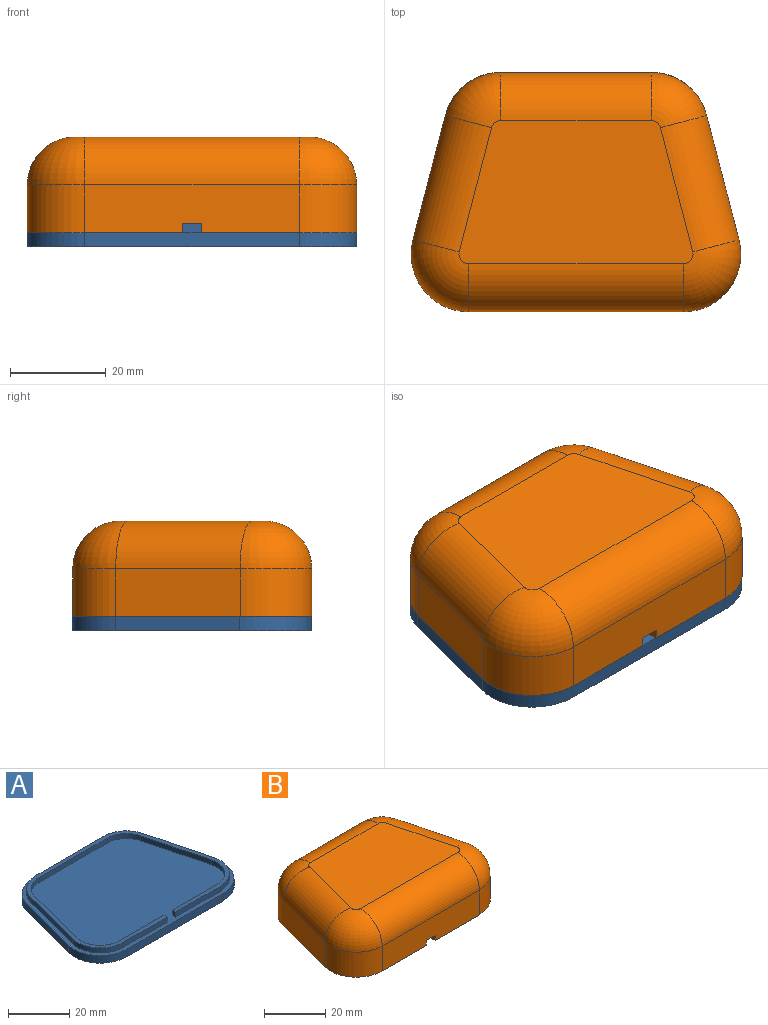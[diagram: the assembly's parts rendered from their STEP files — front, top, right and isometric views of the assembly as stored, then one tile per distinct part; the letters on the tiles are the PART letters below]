
ASSEMBLY  parts=2 mates=1
PART A: 31 faces, bbox 69x50x5 mm
  f0: plane 20.48x2mm, normal (0,-1,0), area 41mm2, adj f2,f12,f14,f30
  f1: plane 20.48x2mm, normal (0,1,0), area 41mm2, adj f2,f12,f26,f29
  f2: plane 65.96x47mm, normal (0,0,1), area 281.1mm2, adj f0,f1,f13,f14,f15,f16,f17,f18
  f3: plane 26x6.76mm, normal (0.97,0.25,0), area 80.6mm2, adj f4,f10,f11,f12
  f4: cylinder r=12mm len=11.61mm, axis (0,0,1), area 47.4mm2, adj f3,f5,f11,f12
  f5: plane 31.44x3mm, normal (0,1,0), area 94.3mm2, adj f4,f6,f11,f12
  f6: cylinder r=12mm len=11.61mm, axis (0,0,1), area 47.4mm2, adj f5,f7,f11,f12
  f7: plane 26x6.76mm, normal (-0.97,0.25,0), area 80.6mm2, adj f6,f8,f11,f12
  f8: cylinder r=12mm len=15.02mm, axis (0,0,1), area 65.7mm2, adj f7,f9,f11,f12
  f9: plane 44.96x3mm, normal (0,-1,0), area 134.9mm2, adj f8,f10,f11,f12
  f10: cylinder r=12mm len=15.02mm, axis (0,0,1), area 65.7mm2, adj f3,f9,f11,f12
  f11: plane 68.96x50mm, normal (0,0,-1), area 3007.2mm2, adj f3,f4,f5,f6,f7,f8,f9,f10
  f12: plane 68.96x50mm, normal (0,0,1), area 2726.1mm2, adj f0,f1,f3,f4,f5,f6,f7,f8
  f13: plane 26x6.76mm, normal (-0.97,0.25,0), area 53.7mm2, adj f2,f12,f14,f28
  f14: cylinder r=10.5mm len=13.14mm, axis (0,0,1), area 38.3mm2, adj f0,f2,f12,f13
  f15: plane 20.48x2mm, normal (0,-1,0), area 41mm2, adj f2,f12,f16,f29
  f16: cylinder r=10.5mm len=13.14mm, axis (0,0,1), area 38.3mm2, adj f2,f12,f15,f17
  f17: plane 26x6.76mm, normal (0.97,0.25,0), area 53.7mm2, adj f2,f12,f16,f18
  f18: cylinder r=10.5mm len=10.16mm, axis (0,0,1), area 27.6mm2, adj f2,f12,f17,f19
  f19: plane 31.44x2mm, normal (0,1,0), area 62.9mm2, adj f2,f12,f18,f28
  f20: cylinder r=9mm len=11.26mm, axis (0,0,1), area 32.9mm2, adj f2,f12,f21,f27
  f21: plane 26x6.76mm, normal (0.97,-0.25,0), area 53.7mm2, adj f2,f12,f20,f22
  f22: cylinder r=9mm len=8.71mm, axis (0,0,1), area 23.7mm2, adj f2,f12,f21,f23
  f23: plane 31.44x2mm, normal (0,-1,0), area 62.9mm2, adj f2,f12,f22,f24
  f24: cylinder r=9mm len=8.71mm, axis (0,0,1), area 23.7mm2, adj f2,f12,f23,f25
  f25: plane 26x6.76mm, normal (-0.97,-0.25,0), area 53.7mm2, adj f2,f12,f24,f26
  f26: cylinder r=9mm len=11.26mm, axis (0,0,1), area 32.9mm2, adj f1,f2,f12,f25
  f27: plane 20.48x2mm, normal (0,1,0), area 41mm2, adj f2,f12,f20,f30
  f28: cylinder r=10.5mm len=10.16mm, axis (0,0,1), area 27.6mm2, adj f2,f12,f13,f19
  f29: plane 2x1.5mm, normal (-1,0,0), area 3mm2, adj f1,f2,f12,f15
  f30: plane 2x1.5mm, normal (1,0,0), area 3mm2, adj f0,f2,f12,f27
PART B: 38 faces, bbox 69x50x20 mm
  f0: plane 68.96x50mm, normal (0,0,-1), area 295.2mm2, adj f1,f2,f3,f4,f5,f6,f7,f8
  f1: plane 44.96x10mm, normal (0,-1,0), area 441.6mm2, adj f0,f8,f9,f18,f35,f36,f37
  f2: plane 44.96x10mm, normal (0,1,0), area 441.6mm2, adj f0,f24,f25,f34,f35,f36,f37
  f3: plane 26x10mm, normal (0.97,0.25,0), area 268.6mm2, adj f0,f4,f9,f14
  f4: cylinder r=12mm len=11.61mm, axis (0,0,-1), area 158mm2, adj f0,f3,f5,f12
  f5: plane 31.44x10mm, normal (0,1,0), area 314.4mm2, adj f0,f4,f6,f11
  f6: cylinder r=12mm len=11.61mm, axis (0,0,-1), area 158mm2, adj f0,f5,f7,f13
  f7: plane 26x10mm, normal (-0.97,0.25,0), area 268.6mm2, adj f0,f6,f8,f15
  f8: cylinder r=12mm len=15.02mm, axis (0,0,-1), area 219mm2, adj f0,f1,f7,f17
  f9: cylinder r=12mm len=15.02mm, axis (0,0,-1), area 219mm2, adj f0,f1,f3,f16
  f10: plane 48.96x30mm, normal (0,0,1), area 1266.1mm2, adj f11,f12,f13,f14,f15,f16,f17,f18
  f11: cylinder r=10mm len=31.44mm, axis (1,0,0), area 493.9mm2, adj f5,f10,f12,f13
  f12: torus R=2mm, axis (0,0,1), area 173mm2, adj f4,f10,f11,f14
  f13: torus R=2mm, axis (0,0,1), area 173mm2, adj f6,f10,f11,f15
  f14: cylinder r=10mm len=28.52mm, axis (0.25,-0.97,0), area 422mm2, adj f3,f10,f12,f16
  f15: cylinder r=10mm len=28.52mm, axis (0.25,0.97,0), area 422mm2, adj f7,f10,f13,f17
  f16: torus R=2mm, axis (0,0,1), area 239.9mm2, adj f9,f10,f14,f18
  f17: torus R=2mm, axis (0,0,1), area 239.9mm2, adj f8,f10,f15,f18
  f18: cylinder r=10mm len=44.96mm, axis (-1,0,0), area 706.3mm2, adj f1,f10,f16,f17
  f19: plane 26x10mm, normal (-0.97,-0.25,0), area 268.6mm2, adj f0,f20,f25,f30
  f20: cylinder r=10.5mm len=10.16mm, axis (0,0,-1), area 138.2mm2, adj f0,f19,f21,f28
  f21: plane 31.44x10mm, normal (0,-1,0), area 314.4mm2, adj f0,f20,f22,f27
  f22: cylinder r=10.5mm len=10.16mm, axis (0,0,-1), area 138.2mm2, adj f0,f21,f23,f29
  f23: plane 26x10mm, normal (0.97,-0.25,0), area 268.6mm2, adj f0,f22,f24,f31
  f24: cylinder r=10.5mm len=13.14mm, axis (0,0,-1), area 191.6mm2, adj f0,f2,f23,f33
  f25: cylinder r=10.5mm len=13.14mm, axis (0,0,-1), area 191.6mm2, adj f0,f2,f19,f32
  f26: plane 48.96x30mm, normal (0,0,-1), area 1266.1mm2, adj f27,f28,f29,f30,f31,f32,f33,f34
  f27: cylinder r=8.5mm len=31.44mm, axis (1,0,0), area 419.8mm2, adj f21,f26,f28,f29
  f28: torus R=2mm, axis (0,0,1), area 130.3mm2, adj f20,f26,f27,f30
  f29: torus R=2mm, axis (0,0,1), area 130.3mm2, adj f22,f26,f27,f31
  f30: cylinder r=8.5mm len=28.14mm, axis (0.25,-0.97,0), area 358.7mm2, adj f19,f26,f28,f32
  f31: cylinder r=8.5mm len=28.14mm, axis (0.25,0.97,0), area 358.7mm2, adj f23,f26,f29,f33
  f32: torus R=2mm, axis (0,0,1), area 180.6mm2, adj f25,f26,f30,f34
  f33: torus R=2mm, axis (0,0,1), area 180.6mm2, adj f24,f26,f31,f34
  f34: cylinder r=8.5mm len=44.96mm, axis (-1,0,0), area 600.3mm2, adj f2,f26,f32,f33
  f35: plane 2x1.5mm, normal (-1,0,0), area 3mm2, adj f0,f1,f2,f36
  f36: plane 4x1.5mm, normal (0,0,-1), area 6mm2, adj f1,f2,f35,f37
  f37: plane 2x1.5mm, normal (1,0,0), area 3mm2, adj f0,f1,f2,f36
PLACE A t=(0,0,7)mm
PLACE B t=(0,-0.13,0)mm
MATE fastened A.f12 <-> B.f0  axis (0,0,1) through (0,0.04,0)mm
